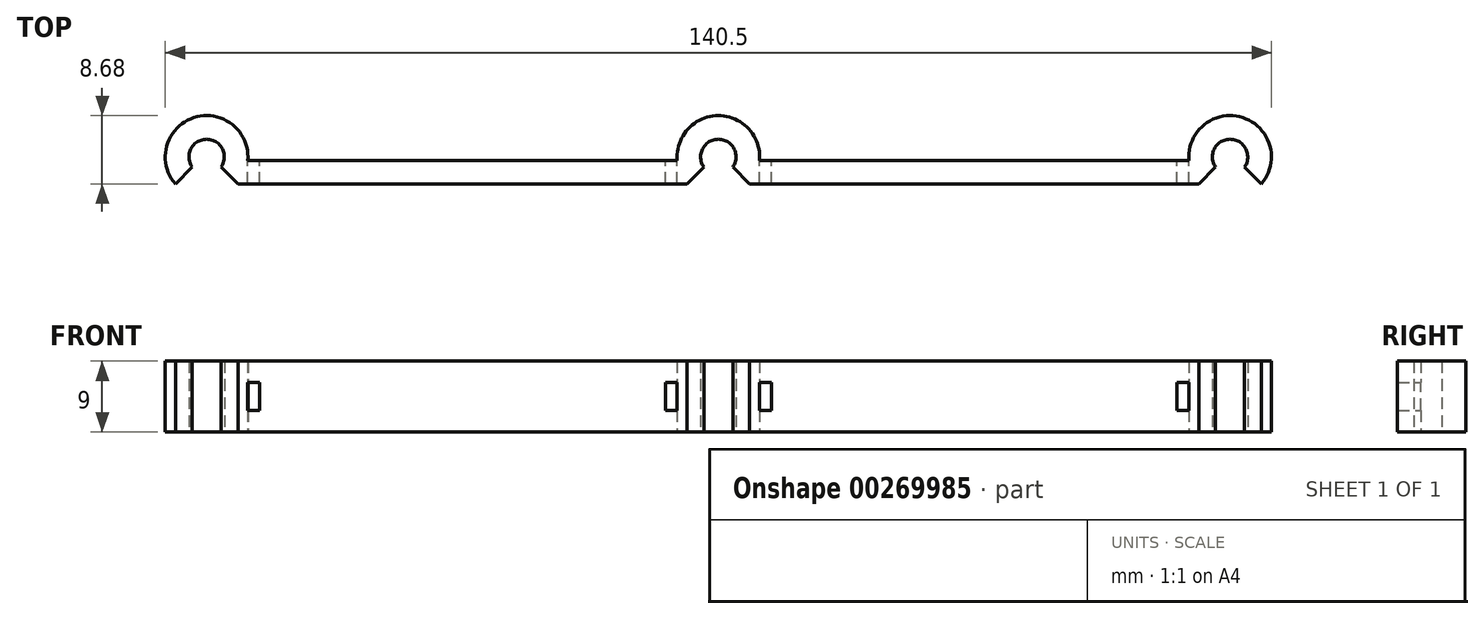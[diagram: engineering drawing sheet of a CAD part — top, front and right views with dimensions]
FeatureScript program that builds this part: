
annotation { "Feature Type Name" : "Feature", "Feature Type Description" : "" }
export const myFeature = defineFeature(function(context is Context, id is Id, definition is map)
    precondition{}
    {
        {
            var Q0;
            Q0=qCreatedBy(makeId("Top.planeOp"),FACE);
            var sketch = newSketch(context, id + "F0", { "sketchPlane" : qUnion([Q0])});
            skArc(sketch, "E0", {"start": v(1.84, -1.3) * mm, "mid": v(0, 2.25) * mm, "end": v(-1.84, -1.3) * mm});
            skLineSegment(sketch, "E1.direction1", {"start": v(0, 0) * mm, "end": v(5.25, 0) * mm, "construction": true});
            skArc(sketch, "E2", {"start": v(3.97, -3.43) * mm, "mid": v(4.92, -1.83) * mm, "end": v(5.25, 0) * mm});
            skPoint(sketch, "E3", {"position": v(-1.84, -1.3) * mm});
            skPoint(sketch, "E4", {"position": v(-3.97, -3.43) * mm});
            skLineSegment(sketch, "E5", {"start": v(-3.97, -3.43) * mm, "end": v(-1.84, -1.3) * mm});
            skLineSegment(sketch, "E6.MirrorCS", {"start": v(3.97, -3.43) * mm, "end": v(1.84, -1.3) * mm});
            skArc(sketch, "E7.1.0.0", {"start": v(70.23, -0.43) * mm, "mid": v(65, 5.25) * mm, "end": v(59.77, -0.43) * mm});
            skLineSegment(sketch, "E7.1.0.1", {"start": v(68.97, -3.43) * mm, "end": v(66.84, -1.3) * mm});
            skArc(sketch, "E7.1.0.2", {"start": v(66.84, -1.3) * mm, "mid": v(65, 2.25) * mm, "end": v(63.16, -1.3) * mm});
            skLineSegment(sketch, "E7.1.0.3", {"start": v(61.03, -3.43) * mm, "end": v(63.16, -1.3) * mm});
            skArc(sketch, "E7.2.0.0", {"start": v(133.97, -3.43) * mm, "mid": v(131.63, 5) * mm, "end": v(124.77, -0.43) * mm});
            skLineSegment(sketch, "E7.2.0.1", {"start": v(133.97, -3.43) * mm, "end": v(131.84, -1.3) * mm});
            skArc(sketch, "E7.2.0.2", {"start": v(131.84, -1.3) * mm, "mid": v(130, 2.25) * mm, "end": v(128.16, -1.3) * mm});
            skLineSegment(sketch, "E7.2.0.3", {"start": v(126.03, -3.43) * mm, "end": v(128.16, -1.3) * mm});
            skLineSegment(sketch, "E7.direction1", {"start": v(-3.97, -3.43) * mm, "end": v(61.03, -3.43) * mm, "construction": true});
            skLineSegment(sketch, "E8", {"start": v(3.97, -3.43) * mm, "end": v(61.03, -3.43) * mm});
            skLineSegment(sketch, "E9", {"start": v(68.97, -3.43) * mm, "end": v(126.03, -3.43) * mm});
            skLineSegment(sketch, "E10", {"start": v(124.77, -0.43) * mm, "end": v(70.23, -0.43) * mm});
            skLineSegment(sketch, "E11.trimOffspring", {"start": v(59.77, -0.43) * mm, "end": v(5.23, -0.43) * mm});
            skArc(sketch, "E12.trimOffspring", {"start": v(5.23, -0.43) * mm, "mid": v(-1.63, 5) * mm, "end": v(-3.97, -3.43) * mm});
            skSolve(sketch);
        }
        {
            var Q0;
            Q0=makeQuery(id+"F0.imprint","IMPRINT",FACE,{"disambiguationData":[TD([[makeQuery(id+"F0.imprint","IMPRINT",EDGE,{"derivedFrom":sQuery(id+"F0.wireOp",EDGE,"E2")}),-1.0]])]});
            var Q1;
            Q1=makeQuery(id+"F0.imprint","IMPRINT",FACE,{"disambiguationData":[TD([[makeQuery(id+"F0.imprint","IMPRINT",EDGE,{"derivedFrom":sQuery(id+"F0.wireOp",EDGE,"E0")}),-1.0]])]});
            extrude(context, id + "F1", {"entities" : qUnion([Q0, Q1]), "depth" : 9 * mm, "offsetDistance" : 25 * mm});
        }
        {
            var Q0;
            Q0=makeQuery(id+"F1.opExtrude","SWEPT_FACE",FACE,{"disambiguationData":[OSD([sQuery(id+"F0.wireOp",EDGE,"E11.trimOffspring")])]});
            var sketch = newSketch(context, id + "F2", { "sketchPlane" : qUnion([Q0])});
            skLineSegment(sketch, "E13.bottom", {"start": v(-6.73, 2.75) * mm, "end": v(-5.23, 2.75) * mm});
            skLineSegment(sketch, "E13.top", {"start": v(-6.73, 6.25) * mm, "end": v(-5.23, 6.25) * mm});
            skLineSegment(sketch, "E13.left", {"start": v(-6.73, 2.75) * mm, "end": v(-6.73, 6.25) * mm});
            skLineSegment(sketch, "E13.right", {"start": v(-5.23, 2.75) * mm, "end": v(-5.23, 6.25) * mm});
            skPoint(sketch, "E13.middle", {"position": v(-5.98, 4.5) * mm});
            skPoint(sketch, "E13.middle.positionSnap0", {"position": v(-5.23, 4.5) * mm});
            skPoint(sketch, "E13.centerSnap0", {"position": v(-5.23, 4.5) * mm});
            skLineSegment(sketch, "E14.1.0.0", {"start": v(-71.73, 2.75) * mm, "end": v(-70.23, 2.75) * mm});
            skLineSegment(sketch, "E14.1.0.1", {"start": v(-71.73, 2.75) * mm, "end": v(-71.73, 6.25) * mm});
            skLineSegment(sketch, "E14.1.0.2", {"start": v(-71.73, 6.25) * mm, "end": v(-70.23, 6.25) * mm});
            skLineSegment(sketch, "E14.1.0.3", {"start": v(-70.23, 2.75) * mm, "end": v(-70.23, 6.25) * mm});
            skLineSegment(sketch, "E14.direction1", {"start": v(-6.73, 2.75) * mm, "end": v(-71.73, 2.75) * mm, "construction": true});
            skLineSegment(sketch, "E15", {"start": v(-59.77, 4.5) * mm, "end": v(-70.23, 4.5) * mm, "construction": true});
            skLineSegment(sketch, "E16", {"start": v(-65, 4.5) * mm, "end": v(-65, 0) * mm, "construction": true});
            skLineSegment(sketch, "E17.MirrorCS", {"start": v(-58.27, 2.75) * mm, "end": v(-58.27, 6.25) * mm});
            skLineSegment(sketch, "E18.MirrorCS", {"start": v(-123.27, 2.75) * mm, "end": v(-58.27, 2.75) * mm, "construction": true});
            skLineSegment(sketch, "E19.MirrorCS", {"start": v(-58.27, 6.25) * mm, "end": v(-59.77, 6.25) * mm});
            skLineSegment(sketch, "E20.bottom", {"start": v(-124.77, 2.75) * mm, "end": v(-123.27, 2.75) * mm});
            skLineSegment(sketch, "E20.top", {"start": v(-124.77, 6.25) * mm, "end": v(-123.27, 6.25) * mm});
            skLineSegment(sketch, "E20.left", {"start": v(-124.77, 2.75) * mm, "end": v(-124.77, 6.25) * mm});
            skLineSegment(sketch, "E20.right", {"start": v(-123.27, 2.75) * mm, "end": v(-123.27, 6.25) * mm});
            skPoint(sketch, "E20.middle", {"position": v(-124.02, 4.5) * mm});
            skLineSegment(sketch, "E21", {"start": v(-59.77, 6.25) * mm, "end": v(-59.77, 2.75) * mm});
            skLineSegment(sketch, "E22", {"start": v(-59.77, 2.75) * mm, "end": v(-58.27, 2.75) * mm});
            skSolve(sketch);
        }
        {
            var Q0;
            Q0=makeQuery(id+"F2.imprint","IMPRINT",FACE,{"disambiguationData":[TD([[makeQuery(id+"F2.imprint","IMPRINT",EDGE,{"derivedFrom":sQuery(id+"F2.wireOp",EDGE,"E17.MirrorCS")}),1.0]])]});
            var Q1;
            Q1=makeQuery(id+"F2.imprint","IMPRINT",FACE,{"disambiguationData":[TD([[makeQuery(id+"F2.imprint","IMPRINT",EDGE,{"derivedFrom":sQuery(id+"F2.wireOp",EDGE,"E14.1.0.0")}),1.0]])]});
            var Q2;
            Q2=makeQuery(id+"F2.imprint","IMPRINT",FACE,{"disambiguationData":[TD([[makeQuery(id+"F2.imprint","IMPRINT",EDGE,{"derivedFrom":sQuery(id+"F2.wireOp",EDGE,"E13.bottom")}),1.0]])]});
            var Q3;
            Q3=makeQuery(id+"F2.imprint","IMPRINT",FACE,{"disambiguationData":[TD([[makeQuery(id+"F2.imprint","IMPRINT",EDGE,{"derivedFrom":sQuery(id+"F2.wireOp",EDGE,"E20.bottom")}),1.0]])]});
            var Q4;
            Q4=makeQuery(id+"F1.opExtrude","SWEPT_FACE",FACE,{"disambiguationData":[OSD([sQuery(id+"F0.wireOp",EDGE,"E9")])]});
            extrude(context, id + "F3", {"entities" : qUnion([Q0, Q1, Q2, Q3]), "operationType" : NewBodyOperationType.REMOVE, "endBound" : BoundingType.UP_TO_SURFACE, "oppositeDirection" : true, "depth" : 25 * mm, "endBoundEntityFace" : qUnion([Q4]), "offsetDistance" : 25 * mm});
        }
    });
